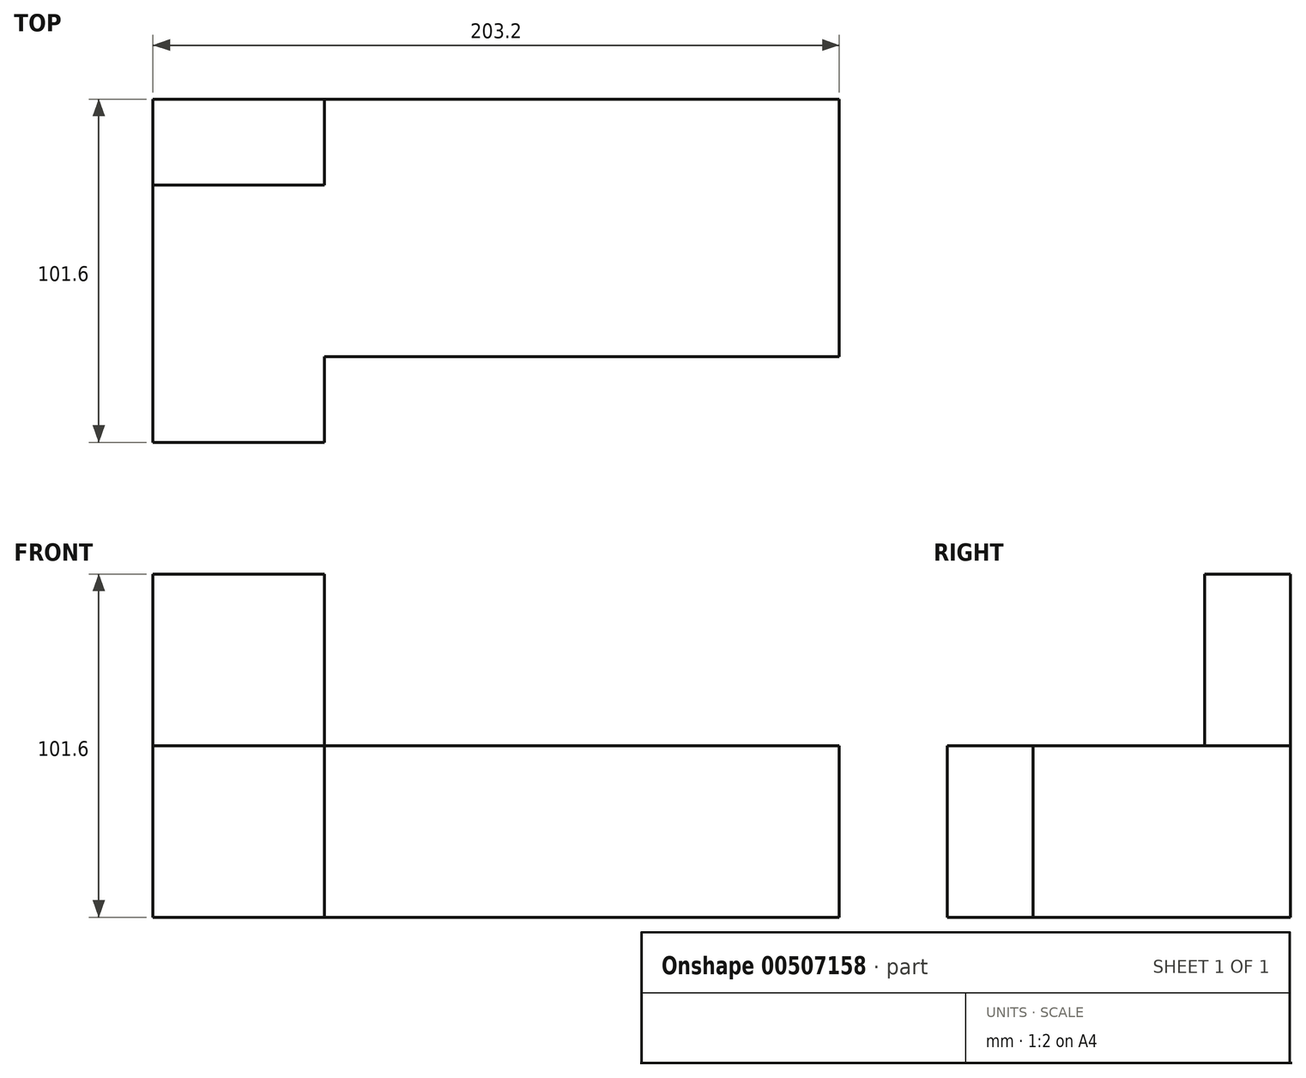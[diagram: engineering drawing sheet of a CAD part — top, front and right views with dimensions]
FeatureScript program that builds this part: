
annotation { "Feature Type Name" : "Feature", "Feature Type Description" : "" }
export const myFeature = defineFeature(function(context is Context, id is Id, definition is map)
    precondition{}
    {
        {
            var Q0;
            Q0=qCreatedBy(makeId("Front.planeOp"),FACE);
            var sketch = newSketch(context, id + "F0", { "sketchPlane" : qUnion([Q0])});
            skLineSegment(sketch, "E0", {"start": v(-93.2, -24.22) * mm, "end": v(110, -24.22) * mm});
            skLineSegment(sketch, "E1", {"start": v(110, -24.22) * mm, "end": v(110, 26.58) * mm});
            skLineSegment(sketch, "E2", {"start": v(110, 26.58) * mm, "end": v(-93.2, 26.58) * mm});
            skLineSegment(sketch, "E3", {"start": v(-93.2, 26.58) * mm, "end": v(-93.2, -24.22) * mm});
            skSolve(sketch);
        }
        {
            var Q0;
            Q0 = qSketchRegion(id + "F0", true);
            extrude(context, id + "F1", {"entities" : qUnion([Q0]), "depth" : 101.6 * mm});
        }
        {
            var Q0;
            Q0=makeQuery(id+"F1.opExtrude","SWEPT_FACE",FACE,{"disambiguationData":[OSD([sQuery(id+"F0.wireOp",EDGE,"E2")])]});
            var sketch = newSketch(context, id + "F2", { "sketchPlane" : qUnion([Q0])});
            skLineSegment(sketch, "E4", {"start": v(110, -76.2) * mm, "end": v(-42.4, -76.2) * mm});
            skLineSegment(sketch, "E5", {"start": v(-42.4, -76.2) * mm, "end": v(-42.4, -101.6) * mm});
            skSolve(sketch);
        }
        {
            var Q0;
            {var subQ0=sQuery(id+"F2.wireOp",EDGE,"E4");Q0=makeQuery(id+"F2.imprint","IMPRINT",FACE,{"disambiguationData":[TD([[makeQuery(id+"F2.imprint","IMPRINT",EDGE,{"derivedFrom":subQ0}),1.0]])]});}
            extrude(context, id + "F3", {"entities" : qUnion([Q0]), "operationType" : NewBodyOperationType.REMOVE, "oppositeDirection" : true, "depth" : 50.8 * mm});
        }
        {
            var Q0;
            Q0=makeQuery(id+"F1.opExtrude","SWEPT_FACE",FACE,{"disambiguationData":[OSD([sQuery(id+"F0.wireOp",EDGE,"E2")])]});
            var sketch = newSketch(context, id + "F4", { "sketchPlane" : qUnion([Q0])});
            skLineSegment(sketch, "E6", {"start": v(-93.2, -25.4) * mm, "end": v(-42.4, -25.4) * mm});
            skLineSegment(sketch, "E7", {"start": v(-42.4, -25.4) * mm, "end": v(-42.4, 0) * mm});
            skSolve(sketch);
        }
        {
            var Q0;
            {var subQ0=sQuery(id+"F4.wireOp",EDGE,"E6");Q0=makeQuery(id+"F4.imprint","IMPRINT",FACE,{"disambiguationData":[TD([[makeQuery(id+"F4.imprint","IMPRINT",EDGE,{"derivedFrom":subQ0}),1.0]])]});}
            extrude(context, id + "F5", {"entities" : qUnion([Q0]), "depth" : 50.8 * mm});
        }
    });
